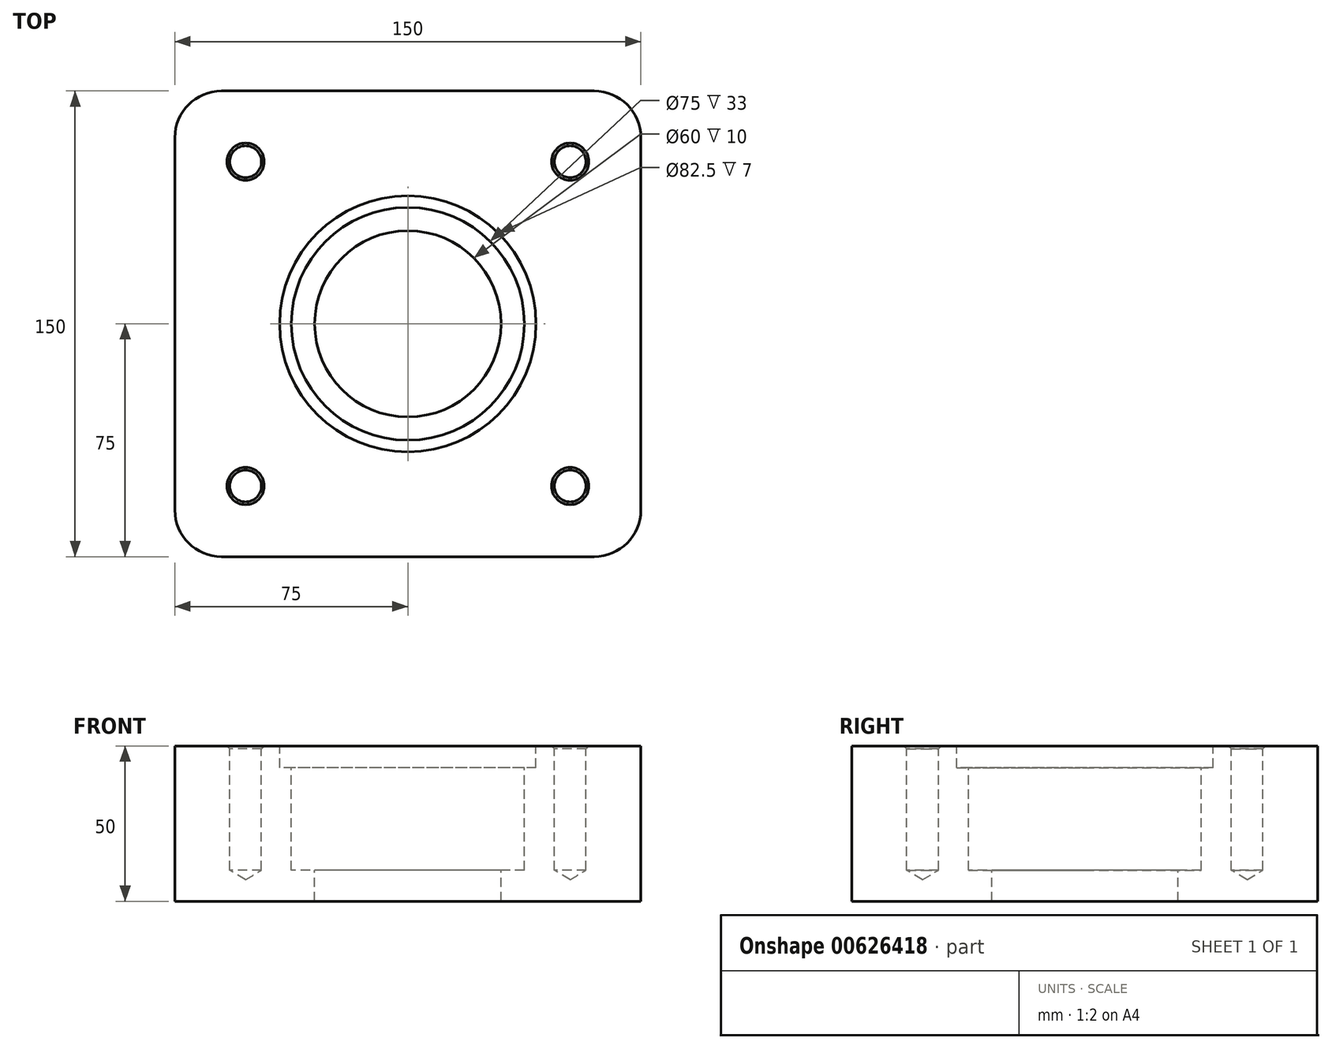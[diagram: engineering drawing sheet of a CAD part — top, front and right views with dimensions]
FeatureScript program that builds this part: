
annotation { "Feature Type Name" : "Feature", "Feature Type Description" : "" }
export const myFeature = defineFeature(function(context is Context, id is Id, definition is map)
    precondition{}
    {
        {
            var Q0;
            Q0=qCreatedBy(makeId("Top.planeOp"),FACE);
            var sketch = newSketch(context, id + "F0", { "sketchPlane" : qUnion([Q0])});
            skLineSegment(sketch, "E0.bottom", {"start": v(-75, 75) * mm, "end": v(75, 75) * mm});
            skLineSegment(sketch, "E0.top", {"start": v(-75, -75) * mm, "end": v(75, -75) * mm});
            skLineSegment(sketch, "E0.left", {"start": v(-75, 75) * mm, "end": v(-75, -75) * mm});
            skLineSegment(sketch, "E0.right", {"start": v(75, 75) * mm, "end": v(75, -75) * mm});
            skPoint(sketch, "E0.middle", {"position": v(0, 0) * mm});
            skCircle(sketch, "E1", {"center": v(0, 0) * mm, "radius": 30 * mm});
            skSolve(sketch);
        }
        {
            var Q0;
            Q0=makeQuery(id+"F0.imprint","IMPRINT",FACE,{"disambiguationData":[TD([[makeQuery(id+"F0.imprint","IMPRINT",EDGE,{"derivedFrom":sQuery(id+"F0.wireOp",EDGE,"E0.bottom")}),-1.0]])]});
            extrude(context, id + "F1", {"entities" : qUnion([Q0]), "oppositeDirection" : true, "depth" : 50 * mm, "offsetDistance" : 25 * mm});
        }
        {
            var Q0;
            Q0=makeQuery(id+"F1.opExtrude","CAP_FACE",FACE,{"disambiguationData":[OSD([sQuery(id+"F0.wireOp",EDGE,"E0.bottom"),sQuery(id+"F0.wireOp",EDGE,"E0.top"),sQuery(id+"F0.wireOp",EDGE,"E0.left"),sQuery(id+"F0.wireOp",EDGE,"E0.right"),sQuery(id+"F0.wireOp",EDGE,"E1")])],"isStart":true});
            var sketch = newSketch(context, id + "F2", { "sketchPlane" : qUnion([Q0])});
            skCircle(sketch, "E2", {"center": v(0, 0) * mm, "radius": 37.5 * mm});
            skSolve(sketch);
        }
        {
            var Q0;
            Q0=makeQuery(id+"F2.imprint","IMPRINT",FACE,{"disambiguationData":[TD([[makeQuery(id+"F2.imprint","IMPRINT",EDGE,{"derivedFrom":sQuery(id+"F2.wireOp",EDGE,"E2")}),1.0]])]});
            extrude(context, id + "F3", {"entities" : qUnion([Q0]), "operationType" : NewBodyOperationType.REMOVE, "oppositeDirection" : true, "depth" : 40 * mm, "offsetDistance" : 25 * mm});
        }
        {
            var Q0;
            Q0=makeQuery(id+"F1.opExtrude","CAP_FACE",FACE,{"disambiguationData":[OSD([sQuery(id+"F0.wireOp",EDGE,"E0.bottom"),sQuery(id+"F0.wireOp",EDGE,"E0.top"),sQuery(id+"F0.wireOp",EDGE,"E0.left"),sQuery(id+"F0.wireOp",EDGE,"E0.right"),sQuery(id+"F0.wireOp",EDGE,"E1")])],"isStart":true});
            var sketch = newSketch(context, id + "F4", { "sketchPlane" : qUnion([Q0])});
            skCircle(sketch, "E3", {"center": v(0, 0) * mm, "radius": 41.25 * mm});
            skSolve(sketch);
        }
        {
            var Q0;
            Q0=makeQuery(id+"F4.imprint","IMPRINT",FACE,{"disambiguationData":[TD([[makeQuery(id+"F4.imprint","IMPRINT",EDGE,{"derivedFrom":sQuery(id+"F4.wireOp",EDGE,"E3")}),1.0]])]});
            extrude(context, id + "F5", {"entities" : qUnion([Q0]), "operationType" : NewBodyOperationType.REMOVE, "oppositeDirection" : true, "depth" : 7 * mm, "offsetDistance" : 25 * mm});
        }
        {
            var Q0;
            Q0=makeQuery(id+"F1.opExtrude","CAP_FACE",FACE,{"disambiguationData":[OSD([sQuery(id+"F0.wireOp",EDGE,"E0.bottom"),sQuery(id+"F0.wireOp",EDGE,"E0.top"),sQuery(id+"F0.wireOp",EDGE,"E0.left"),sQuery(id+"F0.wireOp",EDGE,"E0.right"),sQuery(id+"F0.wireOp",EDGE,"E1")])],"isStart":true});
            var sketch = newSketch(context, id + "F6", { "sketchPlane" : qUnion([Q0])});
            skLineSegment(sketch, "E4.bottom", {"start": v(52.25, 52.25) * mm, "end": v(-52.25, 52.25) * mm});
            skLineSegment(sketch, "E4.top", {"start": v(52.25, -52.25) * mm, "end": v(-52.25, -52.25) * mm});
            skLineSegment(sketch, "E4.left", {"start": v(52.25, 52.25) * mm, "end": v(52.25, -52.25) * mm});
            skLineSegment(sketch, "E4.right", {"start": v(-52.25, 52.25) * mm, "end": v(-52.25, -52.25) * mm});
            skPoint(sketch, "E4.middle", {"position": v(0, 0) * mm});
            skSolve(sketch);
        }
        {
            var Q0;
            Q0=sQuery(id+"F6.wireOp",VERTEX,"E4.right.start");
            var Q1;
            Q1=sQuery(id+"F6.wireOp",VERTEX,"E4.left.start");
            var Q2;
            Q2=sQuery(id+"F6.wireOp",VERTEX,"E4.left.end");
            var Q3;
            Q3=sQuery(id+"F6.wireOp",VERTEX,"E4.right.end");
            var Q4;
            Q4=makeQuery(id+"F1.opExtrude","SWEPT_BODY",BODY,{"disambiguationData":[OSD([sQuery(id+"F0.wireOp",EDGE,"E0.bottom"),sQuery(id+"F0.wireOp",EDGE,"E0.top"),sQuery(id+"F0.wireOp",EDGE,"E0.left"),sQuery(id+"F0.wireOp",EDGE,"E0.right"),sQuery(id+"F0.wireOp",EDGE,"E1")])]});
            hole(context, id + "F7", {"style" : HoleStyle.C_SINK, "endStyle" : HoleEndStyle.BLIND, "holeDiameter" : 10.2 * mm, "cSinkDiameter" : 12 * mm, "cSinkAngle" : 90 * degree, "majorDiameter" : 5 * mm, "holeDepth" : 40 * mm, "isTappedThrough" : true, "tappedDepth" : 12 * mm, "tapClearance" : 3, "locations" : qUnion([Q0, Q1, Q2, Q3]), "scope" : qUnion([Q4])});
        }
        {
            var Q0;
            Q0=makeQuery(id+"F1.opExtrude","SWEPT_EDGE",EDGE,{"disambiguationData":[OSD([sQuery(id+"F0.wireOp",EDGE,"E0.bottom"),sQuery(id+"F0.wireOp",EDGE,"E0.left")])]});
            var Q1;
            Q1=makeQuery(id+"F1.opExtrude","SWEPT_EDGE",EDGE,{"disambiguationData":[OSD([sQuery(id+"F0.wireOp",EDGE,"E0.bottom"),sQuery(id+"F0.wireOp",EDGE,"E0.right")])]});
            var Q2;
            Q2=makeQuery(id+"F1.opExtrude","SWEPT_EDGE",EDGE,{"disambiguationData":[OSD([sQuery(id+"F0.wireOp",EDGE,"E0.top"),sQuery(id+"F0.wireOp",EDGE,"E0.right")])]});
            var Q3;
            Q3=makeQuery(id+"F1.opExtrude","SWEPT_EDGE",EDGE,{"disambiguationData":[OSD([sQuery(id+"F0.wireOp",EDGE,"E0.top"),sQuery(id+"F0.wireOp",EDGE,"E0.left")])]});
            fillet(context, id + "F8", {"entities" : qUnion([Q0, Q1, Q2, Q3]), "radius" : 15 * mm, "tangentPropagation" : true, "allowEdgeOverflow" : false});
        }
    });
